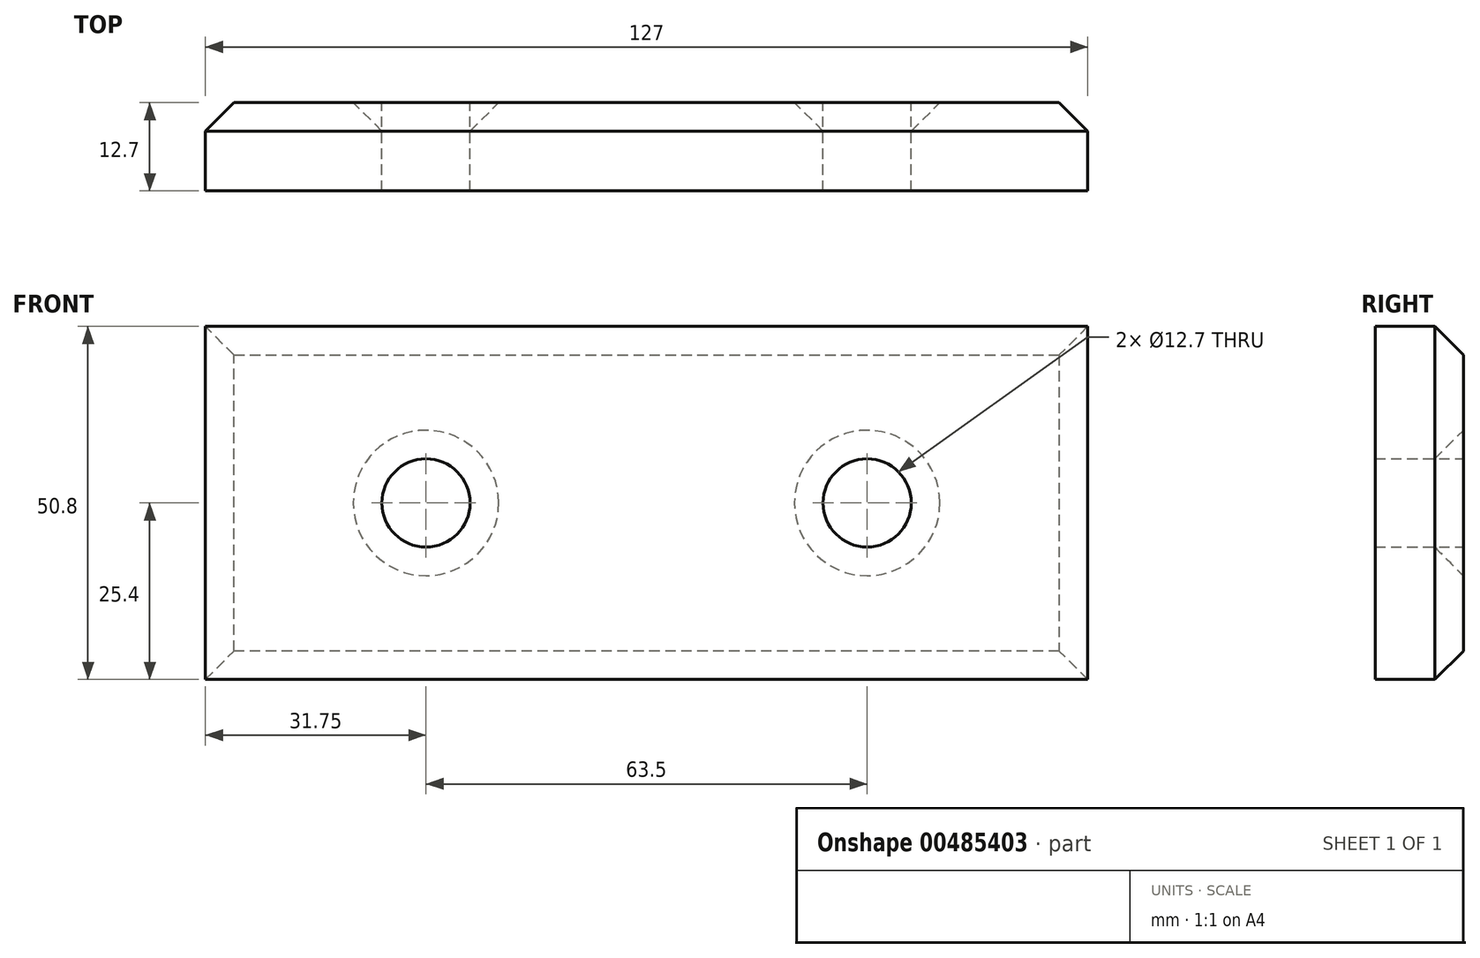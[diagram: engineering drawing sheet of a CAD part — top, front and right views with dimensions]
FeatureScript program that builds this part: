
annotation { "Feature Type Name" : "Feature", "Feature Type Description" : "" }
export const myFeature = defineFeature(function(context is Context, id is Id, definition is map)
    precondition{}
    {
        {
            var Q0;
            Q0=qCreatedBy(makeId("Front.planeOp"),FACE);
            var sketch = newSketch(context, id + "F0", { "sketchPlane" : qUnion([Q0])});
            skLineSegment(sketch, "E0.bottom", {"start": v(63.5, 25.4) * mm, "end": v(-63.5, 25.4) * mm});
            skLineSegment(sketch, "E0.top", {"start": v(63.5, -25.4) * mm, "end": v(-63.5, -25.4) * mm});
            skLineSegment(sketch, "E0.left", {"start": v(63.5, 25.4) * mm, "end": v(63.5, -25.4) * mm});
            skLineSegment(sketch, "E0.right", {"start": v(-63.5, 25.4) * mm, "end": v(-63.5, -25.4) * mm});
            skPoint(sketch, "E0.middle", {"position": v(0, 0) * mm});
            skCircle(sketch, "E1", {"center": v(31.75, 0) * mm, "radius": 6.35 * mm});
            skCircle(sketch, "E2", {"center": v(-31.75, 0) * mm, "radius": 6.35 * mm});
            skSolve(sketch);
        }
        {
            var Q0;
            Q0=makeQuery(id+"F0.imprint","IMPRINT",FACE,{"disambiguationData":[TD([[makeQuery(id+"F0.imprint","IMPRINT",EDGE,{"derivedFrom":sQuery(id+"F0.wireOp",EDGE,"E2")}),1.0]])]});
            var Q1;
            Q1=makeQuery(id+"F0.imprint","IMPRINT",FACE,{"disambiguationData":[TD([[makeQuery(id+"F0.imprint","IMPRINT",EDGE,{"derivedFrom":sQuery(id+"F0.wireOp",EDGE,"E1")}),1.0]])]});
            extrude(context, id + "F1", {"entities" : qUnion([Q0, Q1]), "depth" : 12.7 * mm});
        }
        {
            var Q0;
            Q0=makeQuery(id+"F0.imprint","IMPRINT",FACE,{"disambiguationData":[TD([[makeQuery(id+"F0.imprint","IMPRINT",EDGE,{"derivedFrom":sQuery(id+"F0.wireOp",EDGE,"E0.bottom")}),1.0]])]});
            extrude(context, id + "F2", {"entities" : qUnion([Q0]), "depth" : 12.7 * mm});
        }
        {
            var Q0;
            Q0=makeQuery(id+"F2.opExtrude","CAP_FACE",FACE,{"disambiguationData":[OSD([sQuery(id+"F0.wireOp",EDGE,"E0.bottom"),sQuery(id+"F0.wireOp",EDGE,"E0.top"),sQuery(id+"F0.wireOp",EDGE,"E0.left"),sQuery(id+"F0.wireOp",EDGE,"E0.right"),sQuery(id+"F0.wireOp",EDGE,"E1"),sQuery(id+"F0.wireOp",EDGE,"E2")])],"isStart":true});
            chamfer(context, id + "F3", {"entities" : qUnion([Q0]), "width" : 4.11 * mm, "tangentPropagation" : true});
        }
    });
